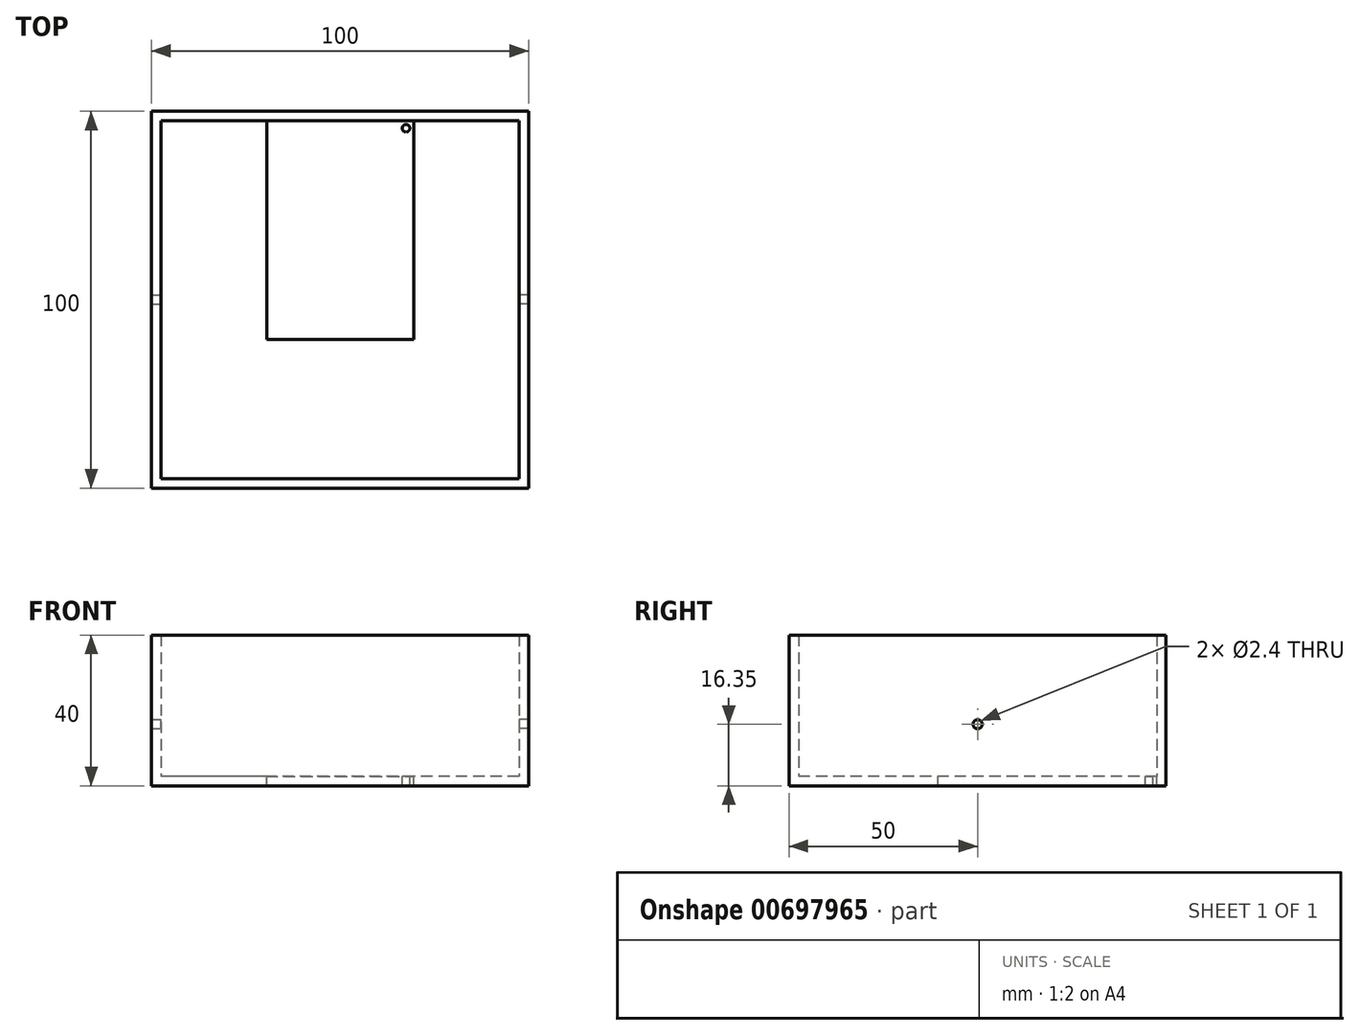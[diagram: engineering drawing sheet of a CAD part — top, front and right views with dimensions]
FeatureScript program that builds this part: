
annotation { "Feature Type Name" : "Feature", "Feature Type Description" : "" }
export const myFeature = defineFeature(function(context is Context, id is Id, definition is map)
    precondition{}
    {
        {
            var Q0;
            Q0=qCreatedBy(makeId("Top.planeOp"),FACE);
            var sketch = newSketch(context, id + "F0", { "sketchPlane" : qUnion([Q0])});
            skLineSegment(sketch, "E0.bottom", {"start": v(50, 50) * mm, "end": v(-50, 50) * mm});
            skLineSegment(sketch, "E0.top", {"start": v(50, -50) * mm, "end": v(-50, -50) * mm});
            skLineSegment(sketch, "E0.left", {"start": v(50, 50) * mm, "end": v(50, -50) * mm});
            skLineSegment(sketch, "E0.right", {"start": v(-50, 50) * mm, "end": v(-50, -50) * mm});
            skPoint(sketch, "E0.middle", {"position": v(0, 0) * mm});
            skSolve(sketch);
        }
        {
            var Q0;
            Q0 = qSketchRegion(id + "F0", true);
            extrude(context, id + "F1", {"entities" : qUnion([Q0]), "depth" : 40 * mm, "offsetDistance" : 25 * mm});
        }
        {
            var Q0;
            Q0=makeQuery(id+"F1.opExtrude","CAP_FACE",FACE,{"disambiguationData":[OSD([sQuery(id+"F0.wireOp",EDGE,"E0.bottom"),sQuery(id+"F0.wireOp",EDGE,"E0.top"),sQuery(id+"F0.wireOp",EDGE,"E0.left"),sQuery(id+"F0.wireOp",EDGE,"E0.right")])],"isStart":false});
            shell(context, id + "F2", {"entities" : qUnion([Q0]), "thickness" : 2.5 * mm});
        }
        {
            var Q0;
            Q0=makeQuery(id+"F2.opShell","OFFSET_FACE",FACE,{"disambiguationData":[OSD([sQuery(id+"F0.wireOp",EDGE,"E0.left")])]});
            var sketch = newSketch(context, id + "F3", { "sketchPlane" : qUnion([Q0])});
            skCircle(sketch, "E1", {"center": v(0, 16.35) * mm, "radius": 1.2 * mm});
            skPoint(sketch, "E1.centerSnap0", {"position": v(0, 2.5) * mm});
            skSolve(sketch);
        }
        {
            var Q0;
            Q0 = qSketchRegion(id + "F3", true);
            extrude(context, id + "F4", {"entities" : qUnion([Q0]), "operationType" : NewBodyOperationType.REMOVE, "endBound" : BoundingType.THROUGH_ALL, "depth" : 25 * mm, "offsetDistance" : 25 * mm});
        }
        {
            var Q0;
            Q0 = qSketchRegion(id + "F3", true);
            extrude(context, id + "F5", {"entities" : qUnion([Q0]), "operationType" : NewBodyOperationType.REMOVE, "oppositeDirection" : true, "depth" : 25 * mm, "offsetDistance" : 25 * mm});
        }
        {
            var Q0;
            Q0=makeQuery(id+"F2.opShell","OFFSET_FACE",FACE,{"disambiguationData":[OSD([sQuery(id+"F0.wireOp",EDGE,"E0.bottom"),sQuery(id+"F0.wireOp",EDGE,"E0.top"),sQuery(id+"F0.wireOp",EDGE,"E0.left"),sQuery(id+"F0.wireOp",EDGE,"E0.right")])]});
            var sketch = newSketch(context, id + "F6", { "sketchPlane" : qUnion([Q0])});
            skLineSegment(sketch, "E2.bottom", {"start": v(-19.5, 47.5) * mm, "end": v(19.5, 47.5) * mm});
            skLineSegment(sketch, "E2.top", {"start": v(-19.5, -10.5) * mm, "end": v(19.5, -10.5) * mm});
            skLineSegment(sketch, "E2.left", {"start": v(-19.5, 47.5) * mm, "end": v(-19.5, -10.5) * mm});
            skLineSegment(sketch, "E2.right", {"start": v(19.5, 47.5) * mm, "end": v(19.5, -10.5) * mm});
            skCircle(sketch, "E3", {"center": v(-17.5, 45.5) * mm, "radius": 1 * mm});
            skCircle(sketch, "E4.MirrorC", {"center": v(17.5, 45.5) * mm, "radius": 1 * mm});
            skCircle(sketch, "E5", {"center": v(-17.5, -8.5) * mm, "radius": 1 * mm});
            skCircle(sketch, "E6", {"center": v(17.5, -8.5) * mm, "radius": 1 * mm});
            skSolve(sketch);
        }
        {
            var Q0;
            Q0=makeQuery(id+"F6.imprint","IMPRINT",FACE,{"disambiguationData":[TD([[makeQuery(id+"F6.imprint","IMPRINT",EDGE,{"derivedFrom":sQuery(id+"F6.wireOp",EDGE,"E5")}),1.0]])]});
            var Q1;
            Q1=makeQuery(id+"F6.imprint","IMPRINT",FACE,{"disambiguationData":[TD([[makeQuery(id+"F6.imprint","IMPRINT",EDGE,{"derivedFrom":sQuery(id+"F6.wireOp",EDGE,"E6")}),1.0]])]});
            var Q2;
            Q2=makeQuery(id+"F6.imprint","IMPRINT",FACE,{"disambiguationData":[TD([[makeQuery(id+"F6.imprint","IMPRINT",EDGE,{"derivedFrom":sQuery(id+"F6.wireOp",EDGE,"E4.MirrorC")}),-1.0]])]});
            var Q3;
            Q3=makeQuery(id+"F6.imprint","IMPRINT",FACE,{"disambiguationData":[TD([[makeQuery(id+"F6.imprint","IMPRINT",EDGE,{"derivedFrom":sQuery(id+"F6.wireOp",EDGE,"E3")}),1.0]])]});
            extrude(context, id + "F7", {"entities" : qUnion([Q0, Q1, Q2, Q3]), "operationType" : NewBodyOperationType.REMOVE, "oppositeDirection" : true, "depth" : 25 * mm, "offsetDistance" : 25 * mm});
        }
    });
